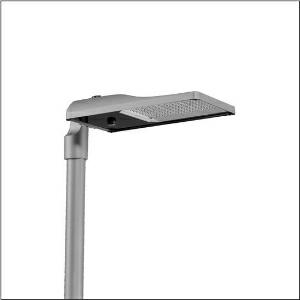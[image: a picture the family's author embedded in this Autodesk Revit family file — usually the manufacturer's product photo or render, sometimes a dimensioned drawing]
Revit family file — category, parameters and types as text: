
# Revit family: streetlight_sl_31_maxi___st0_5a_5xh8b31t08sa_315f
name_source: partatom
category: Lighting Fixtures
units: mm (PartAtom-declared; Revit-internal decimal feet)

## family parameters
Cut with Voids When Loaded = No
Host = Face
Light Source = No
Part Type = Normal
Room Calculation Point = No
Round Connector Dimension = Use Diameter
Shared = No

## types (1)
- --- (1 x LED, 28310 lm, 211.4 W, 3000K)
    Apparent Load = 211 VA
    CIE Flux Codes = 41 75 97 100 100
    Color Rendering = 70
    Color Temperature = 3000K
    Default Elevation = 1800 mm
    Description = Streetlight SL 31 maxi D4i, Desk-Remote mast luminaire for post-top, side-entry; light control with lens of PMMA; light distribution: ST0.5a, direct asymmetric distribution, for standard-compliant lighting for roads and squares; LED: luminous flux: 28.310lm, light colour: 730, colour temperature: 3000K; luminous efficacy: 133,9lm/W; control: pre-setting: logarithmic dimming characteristic, flexible luminous flux parameterisation, time-dependent luminous flux control, constant luminous flux control, power reduction, intelligent temperature release in ECG and LED module, overheat protection; luminaire housing, of diecast aluminium, Siteco® metallic grey (DB 702S), corrosivity category C5 high according to DIN EN ISO 12944; cover of toughened safety glass, transparent, opened without tools; mast flange of diecast aluminium, Siteco® metallic grey (DB 702S), spigot size: 76/60mm, mast flange included unmounted; with cable H07RN-F 2x 1.5mm², cable length: 14,5m, connection cable pre-assembled; mains connection: 220..240V, AC, 50/60Hz; power consumption (at start of service life): 211,4W / (at end of service life): 238W / (with reduced operation 50%): 88,1W; protection rating (complete): IP66; insulation class (complete): insulation class II (safety insulation); impact resistance: IK09; certification: CE, ENEC, ENEC+, VDE, UKCA, ZD4i; permissible operating ambient temperature for outdoor applications: -40..+50°C; packaging unit: 1 piece

Light Distribution: ST0.5a
    Height = 79 mm
    Lamp = 1 x LED
    Lamp Light Flux = 28310 lm
    Lamp Power = 211.4 W
    Lamp count = 1
    Length = 657 mm
    Luminous efficacy = 134 lm/W
    Manufacturer = Siteco
    ModVariant = No
    Model = 5XH8B31T08SA
    Number of Poles = 1
    OnlyDefault = Yes
    Power Factor = 1
    Product Name = Streetlight SL 31 maxi | ST0.5a
    Product group = mast luminaire | pylon top
    ProductGroupID = 6100
    Protection Class = Protection class II
    Protection Degree = IP 66
    RLX_Detail_Level = 1
    RLX_Emergency_Light_Flux = 0 lm
    RLX_Emergency_Type = 0
    RLX_Emergency_Type_DB = No
    RlxData = <blob elided: 58193 chars, md5=9e757c73>
    Socket = socket
    Standby Power = 0 W
    System Light Flux = 28311 lm
    System Power = 211 W
    Type Comments = factory setting: luminous flux: 100 % | dim-lin: 254 | 727 mA
    Type Image = l_1300303.jpg
    URL = http://relux.com
    VarID = @adj_040010
    Voltage = 0 V
    Weight = 0.00 kg
    Width = 362 mm

## geometry (parser evidence)
native form markers: Blend x4, Sweep x12
no freeform markers — native parametric forms only
